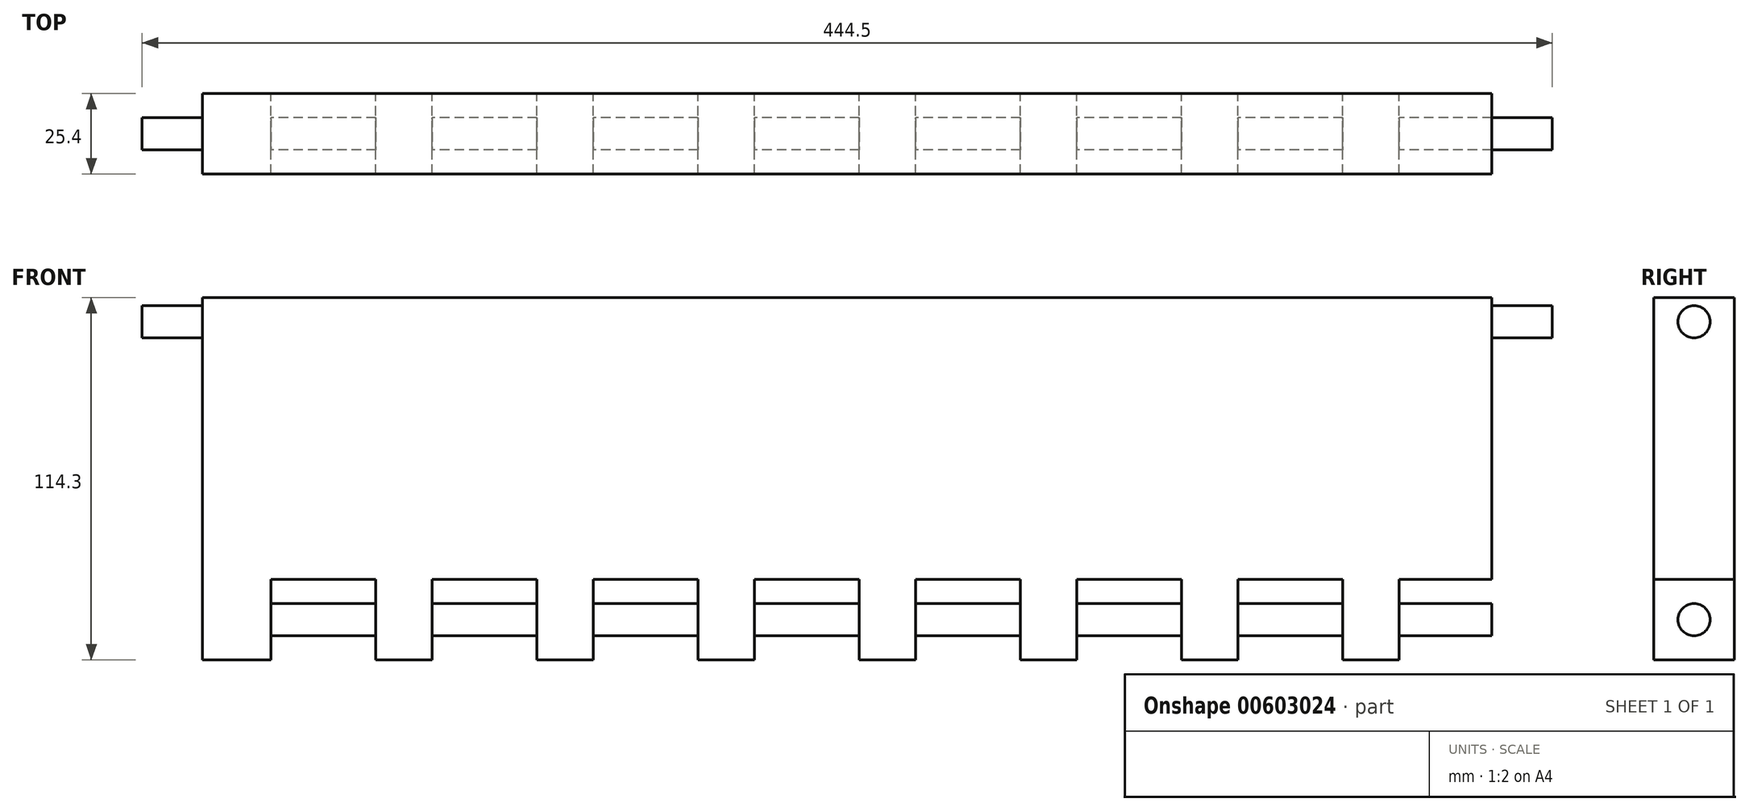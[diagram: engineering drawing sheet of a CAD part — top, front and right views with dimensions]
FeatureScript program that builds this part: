
annotation { "Feature Type Name" : "Feature", "Feature Type Description" : "" }
export const myFeature = defineFeature(function(context is Context, id is Id, definition is map)
    precondition{}
    {
        {
            var Q0;
            Q0=qCreatedBy(makeId("Front.planeOp"),FACE);
            var sketch = newSketch(context, id + "F0", { "sketchPlane" : qUnion([Q0])});
            skLineSegment(sketch, "E0.bottom", {"start": v(203.2, -57.15) * mm, "end": v(-203.2, -57.15) * mm});
            skLineSegment(sketch, "E0.top", {"start": v(203.2, 57.15) * mm, "end": v(-203.2, 57.15) * mm});
            skLineSegment(sketch, "E0.left", {"start": v(203.2, -57.15) * mm, "end": v(203.2, 57.15) * mm});
            skLineSegment(sketch, "E0.right", {"start": v(-203.2, -57.15) * mm, "end": v(-203.2, 57.15) * mm});
            skPoint(sketch, "E0.middle", {"position": v(0, 0) * mm});
            skLineSegment(sketch, "E1", {"start": v(-203.2, -57.15) * mm, "end": v(-203.2, -31.75) * mm});
            skLineSegment(sketch, "E2", {"start": v(-203.2, -31.75) * mm, "end": v(203.2, -31.75) * mm});
            skLineSegment(sketch, "E3", {"start": v(-203.2, -57.15) * mm, "end": v(-177.8, -57.15) * mm});
            skLineSegment(sketch, "E4", {"start": v(-177.8, -57.15) * mm, "end": v(-152.4, -57.15) * mm});
            skLineSegment(sketch, "E5", {"start": v(-152.4, -57.15) * mm, "end": v(-127, -57.15) * mm});
            skLineSegment(sketch, "E6", {"start": v(-127, -57.15) * mm, "end": v(-101.6, -57.15) * mm});
            skLineSegment(sketch, "E7", {"start": v(-101.6, -57.15) * mm, "end": v(-76.2, -57.15) * mm});
            skLineSegment(sketch, "E8", {"start": v(-76.2, -57.15) * mm, "end": v(-50.8, -57.15) * mm});
            skLineSegment(sketch, "E9", {"start": v(-50.8, -57.15) * mm, "end": v(-25.4, -57.15) * mm});
            skLineSegment(sketch, "E10", {"start": v(-25.4, -57.15) * mm, "end": v(0, -57.15) * mm});
            skLineSegment(sketch, "E11", {"start": v(0, -57.15) * mm, "end": v(25.4, -57.15) * mm});
            skLineSegment(sketch, "E12", {"start": v(25.4, -57.15) * mm, "end": v(50.8, -57.15) * mm});
            skLineSegment(sketch, "E13", {"start": v(50.8, -57.15) * mm, "end": v(76.2, -57.15) * mm});
            skLineSegment(sketch, "E14", {"start": v(76.2, -57.15) * mm, "end": v(101.6, -57.15) * mm});
            skLineSegment(sketch, "E15", {"start": v(101.6, -57.15) * mm, "end": v(127, -57.15) * mm});
            skLineSegment(sketch, "E16", {"start": v(127, -57.15) * mm, "end": v(152.4, -57.15) * mm});
            skLineSegment(sketch, "E17", {"start": v(152.4, -57.15) * mm, "end": v(177.8, -57.15) * mm});
            skLineSegment(sketch, "E18", {"start": v(177.8, -57.15) * mm, "end": v(203.2, -57.15) * mm});
            skLineSegment(sketch, "E19", {"start": v(-177.8, -57.15) * mm, "end": v(-177.8, -31.75) * mm});
            skLineSegment(sketch, "E20", {"start": v(-152.4, -57.15) * mm, "end": v(-152.4, -31.75) * mm});
            skLineSegment(sketch, "E21", {"start": v(-127, -57.15) * mm, "end": v(-127, -31.75) * mm});
            skLineSegment(sketch, "E22", {"start": v(-101.6, -57.15) * mm, "end": v(-101.6, -31.75) * mm});
            skLineSegment(sketch, "E23", {"start": v(-76.2, -57.15) * mm, "end": v(-76.2, -31.75) * mm});
            skLineSegment(sketch, "E24", {"start": v(-50.8, -57.15) * mm, "end": v(-50.8, -31.75) * mm});
            skLineSegment(sketch, "E25", {"start": v(-25.4, -57.15) * mm, "end": v(-25.4, -31.75) * mm});
            skLineSegment(sketch, "E26", {"start": v(0, -57.15) * mm, "end": v(0, -31.75) * mm});
            skLineSegment(sketch, "E27", {"start": v(25.4, -57.15) * mm, "end": v(25.4, -31.75) * mm});
            skLineSegment(sketch, "E28", {"start": v(50.8, -57.15) * mm, "end": v(50.8, -31.75) * mm});
            skLineSegment(sketch, "E29", {"start": v(76.2, -57.15) * mm, "end": v(76.2, -31.75) * mm});
            skLineSegment(sketch, "E30", {"start": v(101.6, -57.15) * mm, "end": v(101.6, -31.75) * mm});
            skLineSegment(sketch, "E31", {"start": v(127, -57.15) * mm, "end": v(127, -31.75) * mm});
            skLineSegment(sketch, "E32", {"start": v(152.4, -57.15) * mm, "end": v(152.4, -31.75) * mm});
            skLineSegment(sketch, "E33", {"start": v(177.8, -57.15) * mm, "end": v(177.8, -31.75) * mm});
            skLineSegment(sketch, "E34", {"start": v(-203.2, -57.15) * mm, "end": v(-199.4, -57.15) * mm});
            skLineSegment(sketch, "E35", {"start": v(-199.4, -57.15) * mm, "end": v(-181.6, -57.15) * mm});
            skLineSegment(sketch, "E36", {"start": v(-181.6, -57.15) * mm, "end": v(-177.8, -57.15) * mm});
            skLineSegment(sketch, "E37.1.0.0", {"start": v(-177.8, -57.15) * mm, "end": v(-174, -57.15) * mm});
            skLineSegment(sketch, "E37.1.0.1", {"start": v(-156.21, -57.15) * mm, "end": v(-152.4, -57.15) * mm});
            skLineSegment(sketch, "E37.2.0.0", {"start": v(-152.4, -57.15) * mm, "end": v(-148.6, -57.15) * mm});
            skLineSegment(sketch, "E37.2.0.1", {"start": v(-130.8, -57.15) * mm, "end": v(-127, -57.15) * mm});
            skLineSegment(sketch, "E37.3.0.0", {"start": v(-127, -57.15) * mm, "end": v(-123.2, -57.15) * mm});
            skLineSegment(sketch, "E37.3.0.1", {"start": v(-105.41, -57.15) * mm, "end": v(-101.6, -57.15) * mm});
            skLineSegment(sketch, "E37.4.0.0", {"start": v(-101.6, -57.15) * mm, "end": v(-97.8, -57.15) * mm});
            skLineSegment(sketch, "E37.4.0.1", {"start": v(-80.01, -57.15) * mm, "end": v(-76.2, -57.15) * mm});
            skLineSegment(sketch, "E37.5.0.0", {"start": v(-76.2, -57.15) * mm, "end": v(-72.4, -57.15) * mm});
            skLineSegment(sketch, "E37.5.0.1", {"start": v(-54.61, -57.15) * mm, "end": v(-50.8, -57.15) * mm});
            skLineSegment(sketch, "E37.6.0.0", {"start": v(-50.8, -57.15) * mm, "end": v(-47, -57.15) * mm});
            skLineSegment(sketch, "E37.6.0.1", {"start": v(-29.21, -57.15) * mm, "end": v(-25.4, -57.15) * mm});
            skLineSegment(sketch, "E37.7.0.0", {"start": v(-25.4, -57.15) * mm, "end": v(-21.6, -57.15) * mm});
            skLineSegment(sketch, "E37.7.0.1", {"start": v(-3.81, -57.15) * mm, "end": v(0, -57.15) * mm});
            skLineSegment(sketch, "E37.8.0.0", {"start": v(0, -57.15) * mm, "end": v(3.8, -57.15) * mm});
            skLineSegment(sketch, "E37.8.0.1", {"start": v(21.59, -57.15) * mm, "end": v(25.4, -57.15) * mm});
            skLineSegment(sketch, "E37.9.0.0", {"start": v(25.4, -57.15) * mm, "end": v(29.2, -57.15) * mm});
            skLineSegment(sketch, "E37.9.0.1", {"start": v(46.99, -57.15) * mm, "end": v(50.8, -57.15) * mm});
            skLineSegment(sketch, "E37.10.0.0", {"start": v(50.8, -57.15) * mm, "end": v(54.6, -57.15) * mm});
            skLineSegment(sketch, "E37.10.0.1", {"start": v(72.39, -57.15) * mm, "end": v(76.2, -57.15) * mm});
            skLineSegment(sketch, "E37.11.0.0", {"start": v(76.2, -57.15) * mm, "end": v(80, -57.15) * mm});
            skLineSegment(sketch, "E37.11.0.1", {"start": v(97.79, -57.15) * mm, "end": v(101.6, -57.15) * mm});
            skLineSegment(sketch, "E37.12.0.0", {"start": v(101.6, -57.15) * mm, "end": v(105.4, -57.15) * mm});
            skLineSegment(sketch, "E37.12.0.1", {"start": v(123.19, -57.15) * mm, "end": v(127, -57.15) * mm});
            skLineSegment(sketch, "E37.13.0.0", {"start": v(127, -57.15) * mm, "end": v(130.8, -57.15) * mm});
            skLineSegment(sketch, "E37.13.0.1", {"start": v(148.59, -57.15) * mm, "end": v(152.4, -57.15) * mm});
            skLineSegment(sketch, "E37.14.0.0", {"start": v(152.4, -57.15) * mm, "end": v(156.2, -57.15) * mm});
            skLineSegment(sketch, "E37.14.0.1", {"start": v(173.99, -57.15) * mm, "end": v(177.8, -57.15) * mm});
            skLineSegment(sketch, "E37.15.0.0", {"start": v(177.8, -57.15) * mm, "end": v(181.6, -57.15) * mm});
            skLineSegment(sketch, "E37.15.0.1", {"start": v(199.39, -57.15) * mm, "end": v(203.2, -57.15) * mm});
            skLineSegment(sketch, "E37.direction1", {"start": v(-203.2, -57.15) * mm, "end": v(-177.8, -57.15) * mm, "construction": true});
            skLineSegment(sketch, "E38", {"start": v(-199.4, -57.15) * mm, "end": v(-199.4, -31.75) * mm});
            skLineSegment(sketch, "E39", {"start": v(-181.61, -57.15) * mm, "end": v(-181.61, -31.75) * mm});
            skLineSegment(sketch, "E40.1.0.0", {"start": v(-174, -57.15) * mm, "end": v(-174, -31.75) * mm});
            skLineSegment(sketch, "E40.1.0.1", {"start": v(-156.21, -57.15) * mm, "end": v(-156.21, -31.75) * mm});
            skLineSegment(sketch, "E40.2.0.0", {"start": v(-148.6, -57.15) * mm, "end": v(-148.6, -31.75) * mm});
            skLineSegment(sketch, "E40.2.0.1", {"start": v(-130.8, -57.15) * mm, "end": v(-130.8, -31.75) * mm});
            skLineSegment(sketch, "E40.3.0.0", {"start": v(-123.19, -57.15) * mm, "end": v(-123.19, -31.75) * mm});
            skLineSegment(sketch, "E40.3.0.1", {"start": v(-105.4, -57.15) * mm, "end": v(-105.4, -31.75) * mm});
            skLineSegment(sketch, "E40.4.0.0", {"start": v(-97.79, -57.15) * mm, "end": v(-97.79, -31.75) * mm});
            skLineSegment(sketch, "E40.4.0.1", {"start": v(-80, -57.15) * mm, "end": v(-80, -31.75) * mm});
            skLineSegment(sketch, "E40.5.0.0", {"start": v(-72.39, -57.15) * mm, "end": v(-72.39, -31.75) * mm});
            skLineSegment(sketch, "E40.5.0.1", {"start": v(-54.6, -57.15) * mm, "end": v(-54.6, -31.75) * mm});
            skLineSegment(sketch, "E40.6.0.0", {"start": v(-46.99, -57.15) * mm, "end": v(-46.99, -31.75) * mm});
            skLineSegment(sketch, "E40.6.0.1", {"start": v(-29.2, -57.15) * mm, "end": v(-29.2, -31.75) * mm});
            skLineSegment(sketch, "E40.7.0.0", {"start": v(-21.59, -57.15) * mm, "end": v(-21.59, -31.75) * mm});
            skLineSegment(sketch, "E40.7.0.1", {"start": v(-3.8, -57.15) * mm, "end": v(-3.8, -31.75) * mm});
            skLineSegment(sketch, "E40.8.0.0", {"start": v(3.81, -57.15) * mm, "end": v(3.81, -31.75) * mm});
            skLineSegment(sketch, "E40.8.0.1", {"start": v(21.6, -57.15) * mm, "end": v(21.6, -31.75) * mm});
            skLineSegment(sketch, "E40.9.0.0", {"start": v(29.21, -57.15) * mm, "end": v(29.21, -31.75) * mm});
            skLineSegment(sketch, "E40.9.0.1", {"start": v(47, -57.15) * mm, "end": v(47, -31.75) * mm});
            skLineSegment(sketch, "E40.10.0.0", {"start": v(54.61, -57.15) * mm, "end": v(54.61, -31.75) * mm});
            skLineSegment(sketch, "E40.10.0.1", {"start": v(72.4, -57.15) * mm, "end": v(72.4, -31.75) * mm});
            skLineSegment(sketch, "E40.11.0.0", {"start": v(80.01, -57.15) * mm, "end": v(80.01, -31.75) * mm});
            skLineSegment(sketch, "E40.11.0.1", {"start": v(97.8, -57.15) * mm, "end": v(97.8, -31.75) * mm});
            skLineSegment(sketch, "E40.12.0.0", {"start": v(105.41, -57.15) * mm, "end": v(105.41, -31.75) * mm});
            skLineSegment(sketch, "E40.12.0.1", {"start": v(123.2, -57.15) * mm, "end": v(123.2, -31.75) * mm});
            skLineSegment(sketch, "E40.13.0.0", {"start": v(130.81, -57.15) * mm, "end": v(130.81, -31.75) * mm});
            skLineSegment(sketch, "E40.13.0.1", {"start": v(148.6, -57.15) * mm, "end": v(148.6, -31.75) * mm});
            skLineSegment(sketch, "E40.14.0.0", {"start": v(156.21, -57.15) * mm, "end": v(156.21, -31.75) * mm});
            skLineSegment(sketch, "E40.14.0.1", {"start": v(174, -57.15) * mm, "end": v(174, -31.75) * mm});
            skLineSegment(sketch, "E40.15.0.0", {"start": v(181.61, -57.15) * mm, "end": v(181.61, -31.75) * mm});
            skLineSegment(sketch, "E40.15.0.1", {"start": v(199.4, -57.15) * mm, "end": v(199.4, -31.75) * mm});
            skLineSegment(sketch, "E40.direction1", {"start": v(-199.4, -57.15) * mm, "end": v(-174, -57.15) * mm, "construction": true});
            skSolve(sketch);
        }
        {
            var Q0;
            {var subQ47=sQuery(id+"F0.wireOp",EDGE,"E0.top");Q0=makeQuery(id+"F0.imprint","IMPRINT",FACE,{"disambiguationData":[TD([[makeQuery(id+"F0.imprint","IMPRINT",EDGE,{"derivedFrom":subQ47}),1.0]])]});}
            var Q1;
            {var subQ0=sQuery(id+"F0.wireOp",EDGE,"E38");Q1=makeQuery(id+"F0.imprint","IMPRINT",FACE,{"disambiguationData":[TD([[makeQuery(id+"F0.imprint","IMPRINT",EDGE,{"derivedFrom":subQ0}),-1.0]])]});}
            var Q2;
            {var subQ0=sQuery(id+"F0.wireOp",EDGE,"E40.2.0.0");Q2=makeQuery(id+"F0.imprint","IMPRINT",FACE,{"disambiguationData":[TD([[makeQuery(id+"F0.imprint","IMPRINT",EDGE,{"derivedFrom":subQ0}),-1.0]])]});}
            var Q3;
            {var subQ0=sQuery(id+"F0.wireOp",EDGE,"E40.4.0.0");Q3=makeQuery(id+"F0.imprint","IMPRINT",FACE,{"disambiguationData":[TD([[makeQuery(id+"F0.imprint","IMPRINT",EDGE,{"derivedFrom":subQ0}),-1.0]])]});}
            var Q4;
            {var subQ0=sQuery(id+"F0.wireOp",EDGE,"E40.6.0.0");Q4=makeQuery(id+"F0.imprint","IMPRINT",FACE,{"disambiguationData":[TD([[makeQuery(id+"F0.imprint","IMPRINT",EDGE,{"derivedFrom":subQ0}),-1.0]])]});}
            var Q5;
            {var subQ0=sQuery(id+"F0.wireOp",EDGE,"E40.8.0.0");Q5=makeQuery(id+"F0.imprint","IMPRINT",FACE,{"disambiguationData":[TD([[makeQuery(id+"F0.imprint","IMPRINT",EDGE,{"derivedFrom":subQ0}),-1.0]])]});}
            var Q6;
            {var subQ0=sQuery(id+"F0.wireOp",EDGE,"E40.10.0.0");Q6=makeQuery(id+"F0.imprint","IMPRINT",FACE,{"disambiguationData":[TD([[makeQuery(id+"F0.imprint","IMPRINT",EDGE,{"derivedFrom":subQ0}),-1.0]])]});}
            var Q7;
            {var subQ2=sQuery(id+"F0.wireOp",EDGE,"E40.14.0.0");Q7=makeQuery(id+"F0.imprint","IMPRINT",FACE,{"disambiguationData":[TD([[makeQuery(id+"F0.imprint","IMPRINT",EDGE,{"derivedFrom":subQ2}),-1.0]])]});}
            var Q8;
            {var subQ0=sQuery(id+"F0.wireOp",EDGE,"E40.12.0.0");Q8=makeQuery(id+"F0.imprint","IMPRINT",FACE,{"disambiguationData":[TD([[makeQuery(id+"F0.imprint","IMPRINT",EDGE,{"derivedFrom":subQ0}),-1.0]])]});}
            var Q9;
            {var subQ0=sQuery(id+"F0.wireOp",EDGE,"E38");Q9=makeQuery(id+"F0.imprint","IMPRINT",FACE,{"disambiguationData":[TD([[makeQuery(id+"F0.imprint","IMPRINT",EDGE,{"derivedFrom":subQ0}),1.0]])]});}
            extrude(context, id + "F1", {"entities" : qUnion([Q0, Q1, Q2, Q3, Q4, Q5, Q6, Q7, Q8, Q9]), "depth" : 25.4 * mm, "offsetDistance" : 25.4 * mm});
        }
        {
            var Q0;
            Q0=makeQuery(id+"F1.opExtrude","SWEPT_FACE",FACE,{"disambiguationData":[OSD([sQuery(id+"F0.wireOp",EDGE,"E0.right")])]});
            var sketch = newSketch(context, id + "F2", { "sketchPlane" : qUnion([Q0])});
            skLineSegment(sketch, "E41", {"start": v(12.7, -57.15) * mm, "end": v(12.7, -44.45) * mm});
            skCircle(sketch, "E42", {"center": v(12.7, -44.45) * mm, "radius": 5.08 * mm});
            skSolve(sketch);
        }
        {
            var Q0;
            Q0 = qSketchRegion(id + "F2", true);
            extrude(context, id + "F3", {"entities" : qUnion([Q0]), "operationType" : NewBodyOperationType.ADD, "oppositeDirection" : true, "depth" : 406.4 * mm, "offsetDistance" : 25.4 * mm});
        }
        {
            var Q0;
            Q0=makeQuery(id+"F1.opExtrude","SWEPT_FACE",FACE,{"disambiguationData":[OSD([sQuery(id+"F0.wireOp",EDGE,"E0.right")])]});
            var sketch = newSketch(context, id + "F4", { "sketchPlane" : qUnion([Q0])});
            skLineSegment(sketch, "E43", {"start": v(12.7, 57.15) * mm, "end": v(12.7, 49.53) * mm});
            skCircle(sketch, "E44", {"center": v(12.7, 49.53) * mm, "radius": 5.08 * mm});
            skSolve(sketch);
        }
        {
            var Q0;
            Q0 = qSketchRegion(id + "F4", true);
            extrude(context, id + "F5", {"entities" : qUnion([Q0]), "operationType" : NewBodyOperationType.ADD, "depth" : 19.05 * mm, "offsetDistance" : 25.4 * mm, "hasSecondDirection" : true, "secondDirectionOppositeDirection" : true, "secondDirectionDepth" : 425.45 * mm});
        }
    });
